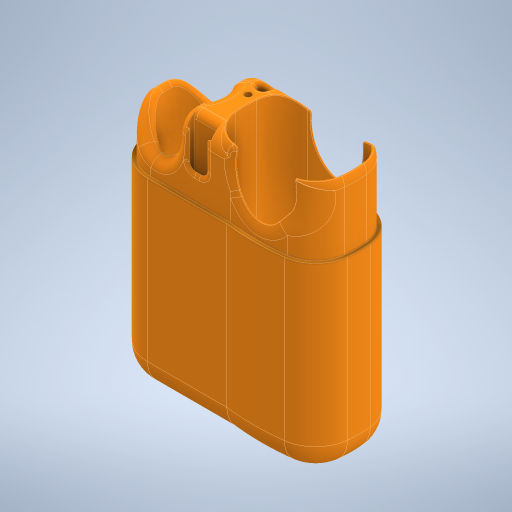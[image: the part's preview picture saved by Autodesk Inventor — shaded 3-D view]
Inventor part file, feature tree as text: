
AUTODESK INVENTOR PART (.ipt)
format: ipt  version: 2023 (Build 270158030, 158C)  size: 1,742,848 bytes
history: native  units: mm
features: fillet x17, extrude x16, sketch x16, projected_geometry x7, other x4, plane x1
ambient origin geometry x8: Origin, YZ Plane, XZ Plane, XY Plane, X Axis, Y Axis, Z Axis, Center Point
bodies: Body1 (feature_tree), Body2 (feature_tree), Body3 (feature_tree), Body4 (feature_tree)
feature tree (61):
  other  "vape"
  extrude  "Extrusion1"  Depth=8.35mm
  fillet  "Fillet1"  Radius=70.0mm
  extrude  "Extrusion2"  Depth=11.6mm TaperAngle=0.0deg
  plane  "Work Plane1"
  extrude  "Extrusion3"  Depth=45.8mm TaperAngle=0.0deg
  extrude  "Extrusion4"  Depth=22.1mm
  extrude  "Extrusion5"  Depth=1.5mm
  extrude  "Extrusion6"  Depth=1.5mm
  fillet  "Fillet2"  Radius=1.5mm
  extrude  "Extrusion7"  Depth=15.55mm
  extrude  "Extrusion8"  Depth=3.0mm
  fillet  "Fillet3"  Radius=3.0mm
  fillet  "Fillet4"  Radius=3.0mm
  extrude  "Extrusion9"  Depth=15.55mm
  fillet  "Fillet5"  Radius=2.0mm
  fillet  "Fillet6"  Radius=13.0mm
  fillet  "Fillet9"  Radius=2.0mm
  extrude  "Extrusion10"  Depth=11.0mm
  extrude  "Extrusion11"  Depth=20.0mm TaperAngle=0.0deg
  fillet  "Fillet10"  Radius=4.0mm
  extrude  "Extrusion13"  Depth=8.0mm
  extrude  "Extrusion14"  Depth=10.0mm
  extrude  "Extrusion15"  Depth=17.0mm
  fillet  "Fillet13"  [1 undecoded]
  fillet  "Fillet14"  Radius=8.0mm
  extrude  "Extrusion16"  Depth=10.0mm
  fillet  "Fillet15"  Radius=6.0mm
  fillet  "Fillet16"  Radius=3.0mm
  fillet  "Fillet17"  Radius=2.9mm
  fillet  "Fillet18"  Radius=5.0mm
  fillet  "Fillet19"  Radius=24.5mm
  extrude  "Extrusion17"  Depth=62.0mm TaperAngle=0.0deg
  fillet  "Fillet20"  Radius=2.4mm
  fillet  "Fillet21"  Radius=7.3mm
  sketch  "Sketch1"  dims[d4=98.5mm d5=0.0mm d9=8.35mm d22=70.0mm d23=0.0mm]
  sketch  "Sketch2"  dims[d24=20.0mm d26=11.6mm d27=0.0mm]
  other  "vape-tube"
  sketch  "Sketch3"  dims[d28=16.0mm d29=45.8mm d30=0.0mm]
  other  "storage"
  sketch  "Sketch4"  dims[d31=16.0mm d38=22.1mm]
  sketch  "Sketch5"  dims[d39=31.1mm d41=1.5mm]
  projected_geometry  "Projected Loop2"
  sketch  "Sketch6"  dims[d42=1.5mm d44=1.5mm d45=1.5mm]
  projected_geometry  "Projected Loop3"
  projected_geometry  "Projected Loop4"
  sketch  "Sketch7"  dims[d46=11.05mm d47=15.55mm]
  projected_geometry  "Projected Loop5"
  sketch  "Sketch8"  dims[d48=3.0mm d49=3.0mm d50=3.0mm d51=3.0mm]
  projected_geometry  "Projected Loop6"
  sketch  "Sketch9"  dims[d52=11.05mm d53=15.55mm d54=2.0mm d55=13.0mm]
  sketch  "Sketch10"  dims[d56=12.5mm d57=60.0mm d58=0.0mm d59=2.0mm]
  sketch  "Sketch11"  dims[d60=10.0mm d61=0.0mm d62=11.0mm]
  sketch  "Sketch13"  dims[d63=1.0mm d64=20.0mm d65=0.0mm d66=4.0mm d67=0.0mm]
  sketch  "Sketch14"  dims[d68=5.0mm d69=8.0mm]
  projected_geometry  "Projected Loop7"
  sketch  "Sketch15"  dims[d70=0.0mm d71=10.0mm]
  projected_geometry  "Projected Loop8"
  other  "vape-lid"
  sketch  "Sketch16"  dims[d72=7.0mm d73=17.0mm d74=0.0mm d75=0.0mm d76=8.0mm]
  sketch  "Sketch17"  dims[d77=2.0mm d80=10.0mm d81=6.0mm d82=3.0mm d83=2.9mm d84=5.0mm d85=24.5mm d86=62.0mm d87=0.0mm d88=2.4mm d89=7.3mm d90=0.5mm d91=8.7mm d92=36.0mm d93=0.0mm d94=1.0mm d103=2.0mm d104=3.0mm d105=71.0mm d106=0.0mm d107=0.05mm d108=71.0mm d109=0.0mm d110=3.0mm d111=30.0deg d112=1.5mm d113=1.5mm d114=1.0mm d115=1.0mm d116=10.0mm d117=10.0mm d118=0.0mm d119=2.0mm d120=2.0mm d121=0.2mm d122=0.2mm d123=0.2mm d124=16.0mm d125=6.0mm d126=10.0mm d127=0.0mm d128=6.8mm d129=2.0mm d130=0.2mm d131=1.0mm]
note: 1 required parameter value undecoded (feature->parameter linkage not recoverable at this tier; creation-order binding heuristic only, values carry confidence <= 0.55)
